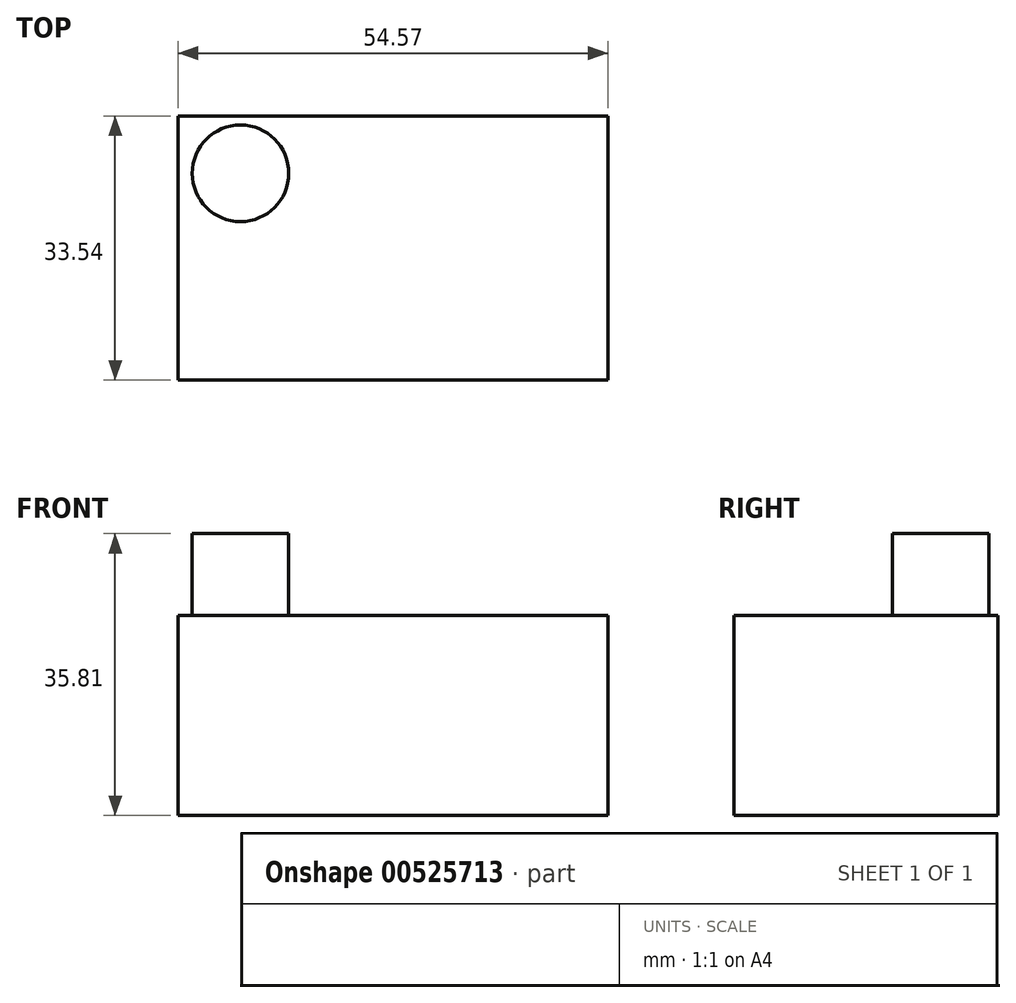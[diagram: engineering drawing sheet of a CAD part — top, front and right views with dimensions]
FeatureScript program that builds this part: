
annotation { "Feature Type Name" : "Feature", "Feature Type Description" : "" }
export const myFeature = defineFeature(function(context is Context, id is Id, definition is map)
    precondition{}
    {
        {
            var Q0;
            Q0=qCreatedBy(makeId("Top.planeOp"),FACE);
            var sketch = newSketch(context, id + "F0", { "sketchPlane" : qUnion([Q0])});
            skLineSegment(sketch, "E0.bottom", {"start": v(0, 0) * mm, "end": v(54.57, 0) * mm});
            skLineSegment(sketch, "E0.top", {"start": v(0, 33.54) * mm, "end": v(54.57, 33.54) * mm});
            skLineSegment(sketch, "E0.left", {"start": v(0, 0) * mm, "end": v(0, 33.54) * mm});
            skLineSegment(sketch, "E0.right", {"start": v(54.57, 0) * mm, "end": v(54.57, 33.54) * mm});
            skSolve(sketch);
        }
        {
            var Q0;
            Q0 = qSketchRegion(id + "F0", true);
            extrude(context, id + "F1", {"entities" : qUnion([Q0]), "depth" : 25.4 * mm, "offsetDistance" : 25.4 * mm});
        }
        {
            var Q0;
            Q0=qCreatedBy(makeId("Top.planeOp"),FACE);
            var sketch = newSketch(context, id + "F2", { "sketchPlane" : qUnion([Q0])});
            skCircle(sketch, "E1", {"center": v(7.9, 26.26) * mm, "radius": 6.13 * mm});
            skSolve(sketch);
        }
        {
            var Q0;
            Q0 = qSketchRegion(id + "F2", true);
            extrude(context, id + "F3", {"entities" : qUnion([Q0]), "operationType" : NewBodyOperationType.ADD, "depth" : 35.81 * mm, "offsetDistance" : 25.4 * mm});
        }
    });
